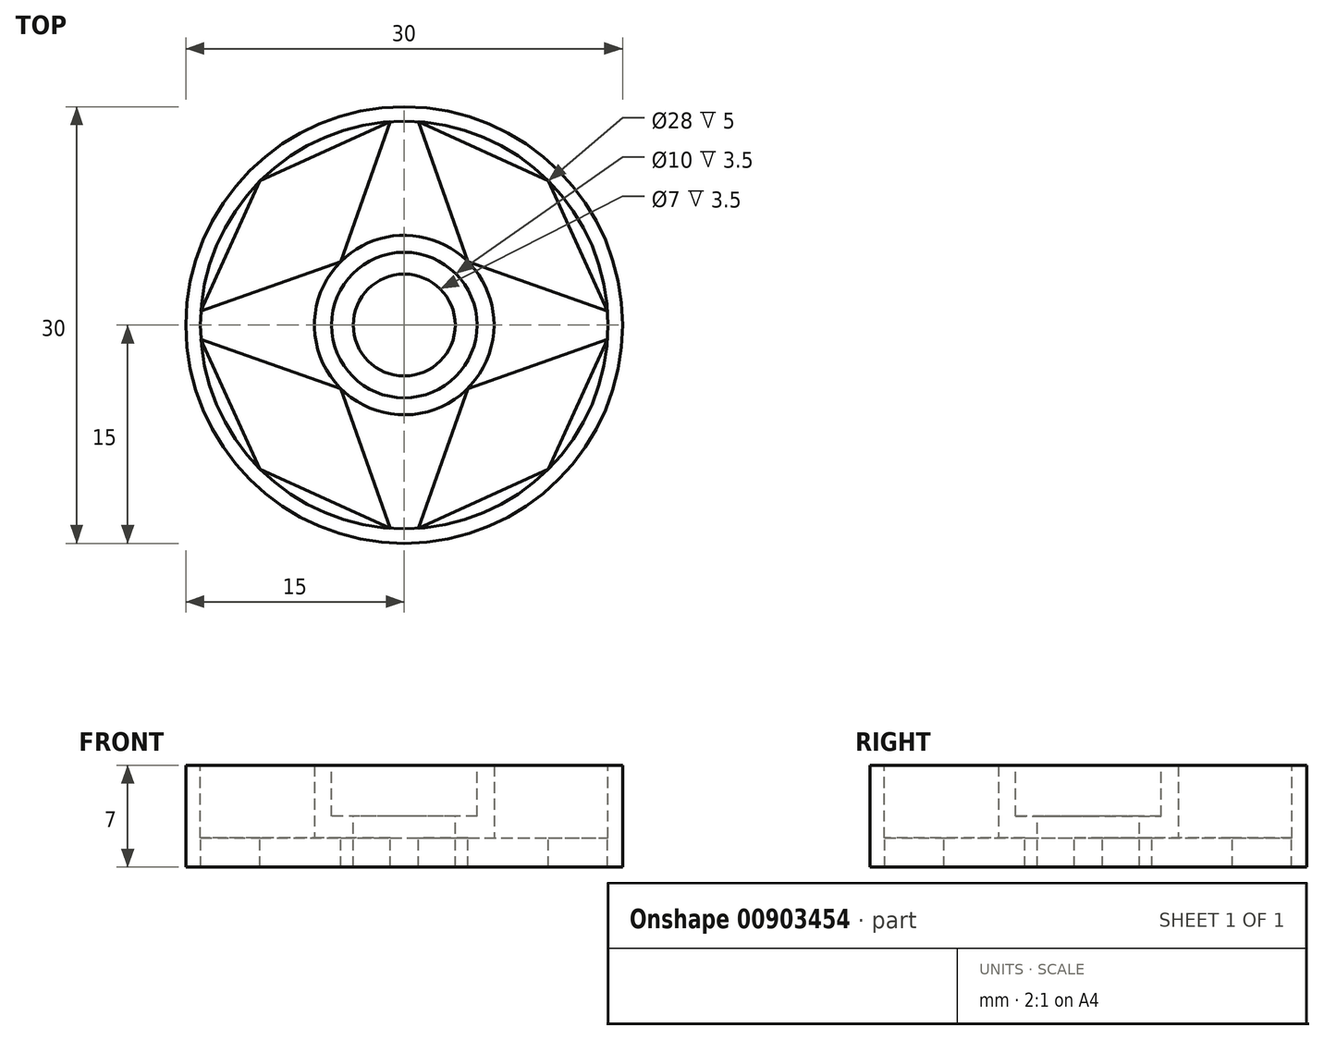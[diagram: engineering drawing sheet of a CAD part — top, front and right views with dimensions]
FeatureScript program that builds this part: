
annotation { "Feature Type Name" : "Feature", "Feature Type Description" : "" }
export const myFeature = defineFeature(function(context is Context, id is Id, definition is map)
    precondition{}
    {
        {
            var Q0;
            Q0=qCreatedBy(makeId("Top.planeOp"),FACE);
            var sketch = newSketch(context, id + "F0", { "sketchPlane" : qUnion([Q0])});
            skCircle(sketch, "E0", {"center": v(0, 0) * mm, "radius": 15 * mm});
            skSolve(sketch);
        }
        {
            var Q0;
            Q0 = qSketchRegion(id + "F0", true);
            extrude(context, id + "F1", {"entities" : qUnion([Q0]), "depth" : 7 * mm, "offsetDistance" : 25 * mm});
        }
        {
            var Q0;
            Q0=makeQuery(id+"F1.opExtrude","CAP_FACE",FACE,{"disambiguationData":[OSD([sQuery(id+"F0.wireOp",EDGE,"E0")])],"isStart":false});
            var sketch = newSketch(context, id + "F2", { "sketchPlane" : qUnion([Q0])});
            skCircle(sketch, "E1", {"center": v(0, 0) * mm, "radius": 14 * mm});
            skSolve(sketch);
        }
        {
            var Q0;
            Q0=makeQuery(id+"F2.imprint","IMPRINT",FACE,{"disambiguationData":[TD([[makeQuery(id+"F2.imprint","IMPRINT",EDGE,{"derivedFrom":sQuery(id+"F2.wireOp",EDGE,"E1")}),1.0]])]});
            extrude(context, id + "F3", {"entities" : qUnion([Q0]), "operationType" : NewBodyOperationType.REMOVE, "oppositeDirection" : true, "depth" : 5 * mm, "offsetDistance" : 25 * mm});
        }
        {
            var Q0;
            Q0=makeQuery(id+"F3.boolean.opBoolean","COPY",FACE,{"derivedFrom":makeQuery(id+"F3.opExtrude","CAP_FACE",FACE,{"disambiguationData":[OSD([sQuery(id+"F2.wireOp",EDGE,"E1")])],"isStart":false})});
            var sketch = newSketch(context, id + "F4", { "sketchPlane" : qUnion([Q0])});
            skCircle(sketch, "E2", {"center": v(0, 0) * mm, "radius": 6.17 * mm});
            skSolve(sketch);
        }
        {
            var Q0;
            Q0=makeQuery(id+"F4.imprint","IMPRINT",FACE,{"disambiguationData":[TD([[makeQuery(id+"F4.imprint","IMPRINT",EDGE,{"derivedFrom":sQuery(id+"F4.wireOp",EDGE,"E2")}),1.0]])]});
            extrude(context, id + "F5", {"entities" : qUnion([Q0]), "operationType" : NewBodyOperationType.ADD, "depth" : 5 * mm, "offsetDistance" : 25 * mm});
        }
        {
            var Q0;
            Q0=makeQuery(id+"F5.opExtrude","CAP_FACE",FACE,{"disambiguationData":[OSD([sQuery(id+"F4.wireOp",EDGE,"E2")])],"isStart":false});
            var sketch = newSketch(context, id + "F6", { "sketchPlane" : qUnion([Q0])});
            skCircle(sketch, "E3", {"center": v(0, 0) * mm, "radius": 5 * mm});
            skSolve(sketch);
        }
        {
            var Q0;
            Q0=makeQuery(id+"F6.imprint","IMPRINT",FACE,{"disambiguationData":[TD([[makeQuery(id+"F6.imprint","IMPRINT",EDGE,{"derivedFrom":sQuery(id+"F6.wireOp",EDGE,"E3")}),1.0]])]});
            extrude(context, id + "F7", {"entities" : qUnion([Q0]), "operationType" : NewBodyOperationType.REMOVE, "oppositeDirection" : true, "depth" : 3.5 * mm, "offsetDistance" : 25 * mm});
        }
        {
            var Q0;
            Q0=makeQuery(id+"F7.boolean.opBoolean","COPY",FACE,{"derivedFrom":makeQuery(id+"F7.opExtrude","CAP_FACE",FACE,{"disambiguationData":[OSD([sQuery(id+"F6.wireOp",EDGE,"E3")])],"isStart":false})});
            var sketch = newSketch(context, id + "F8", { "sketchPlane" : qUnion([Q0])});
            skCircle(sketch, "E4", {"center": v(0, 0) * mm, "radius": 3.5 * mm});
            skSolve(sketch);
        }
        {
            var Q0;
            Q0=makeQuery(id+"F8.imprint","IMPRINT",FACE,{"disambiguationData":[TD([[makeQuery(id+"F8.imprint","IMPRINT",EDGE,{"derivedFrom":sQuery(id+"F8.wireOp",EDGE,"E4")}),1.0]])]});
            extrude(context, id + "F9", {"entities" : qUnion([Q0]), "operationType" : NewBodyOperationType.REMOVE, "endBound" : BoundingType.UP_TO_NEXT, "oppositeDirection" : true, "depth" : 25 * mm, "offsetDistance" : 25 * mm});
        }
        {
            var Q0;
            Q0=makeQuery(id+"F3.boolean.opBoolean","COPY",FACE,{"derivedFrom":makeQuery(id+"F3.opExtrude","CAP_FACE",FACE,{"disambiguationData":[OSD([sQuery(id+"F2.wireOp",EDGE,"E1")])],"isStart":false})});
            var sketch = newSketch(context, id + "F10", { "sketchPlane" : qUnion([Q0])});
            skLineSegment(sketch, "E5", {"start": v(4.36, 4.36) * mm, "end": v(0.97, 13.97) * mm});
            skLineSegment(sketch, "E6.MirrorCS", {"start": v(-4.36, 4.36) * mm, "end": v(-0.97, 13.97) * mm});
            skLineSegment(sketch, "E7.MirrorCS", {"start": v(-4.36, -4.36) * mm, "end": v(-0.97, -13.97) * mm});
            skLineSegment(sketch, "E8.MirrorCS", {"start": v(4.36, -4.36) * mm, "end": v(0.97, -13.97) * mm});
            skLineSegment(sketch, "E9.MirrorCS", {"start": v(4.36, -4.36) * mm, "end": v(13.97, -0.97) * mm});
            skLineSegment(sketch, "E10.MirrorCS", {"start": v(4.36, 4.36) * mm, "end": v(13.97, 0.97) * mm});
            skLineSegment(sketch, "E11.MirrorCS", {"start": v(-4.36, -4.36) * mm, "end": v(-13.97, -0.97) * mm});
            skLineSegment(sketch, "E12.MirrorCS", {"start": v(-4.36, 4.36) * mm, "end": v(-13.97, 0.97) * mm});
            skLineSegment(sketch, "E13", {"start": v(13.97, 0.97) * mm, "end": v(9.9, 9.9) * mm});
            skLineSegment(sketch, "E14", {"start": v(9.9, 9.9) * mm, "end": v(0.97, 13.97) * mm});
            skLineSegment(sketch, "E15.MirrorCS", {"start": v(-9.9, 9.9) * mm, "end": v(-0.97, 13.97) * mm});
            skLineSegment(sketch, "E16.MirrorCS", {"start": v(-13.97, 0.97) * mm, "end": v(-9.9, 9.9) * mm});
            skLineSegment(sketch, "E17.MirrorCS", {"start": v(-9.9, -9.9) * mm, "end": v(-13.97, -0.97) * mm});
            skLineSegment(sketch, "E18.MirrorCS", {"start": v(-0.97, -13.97) * mm, "end": v(-9.9, -9.9) * mm});
            skLineSegment(sketch, "E19.MirrorCS", {"start": v(9.9, -9.9) * mm, "end": v(13.97, -0.97) * mm});
            skLineSegment(sketch, "E20.MirrorCS", {"start": v(0.97, -13.97) * mm, "end": v(9.9, -9.9) * mm});
            skSolve(sketch);
        }
        {
            var Q0;
            Q0 = qSketchRegion(id + "F10", true);
            extrude(context, id + "F11", {"entities" : qUnion([Q0]), "operationType" : NewBodyOperationType.REMOVE, "endBound" : BoundingType.UP_TO_NEXT, "oppositeDirection" : true, "depth" : 25 * mm, "offsetDistance" : 25 * mm});
        }
    });
